# Revit family: ES – eSconce
name_source: partatom
category: Lighting Fixtures
revit_build: Autodesk Revit 2013 (Build: 20120221_2030(x64)
units: mm (PartAtom-declared; Revit-internal decimal feet)

## types (8) — shared parameters
Apparent Load = 55 VA
Default Elevation = 4' - 0"
Description = AAL's eSconce®, is has the flexibility to complement a wide range of architecture for use in both exterior/interior environments.
Glass = Hubbell - Glass
IES File Link = http://www.aal.net
Input Power = 55 W
Lamp = LED
Load Classification = Lighting
Manufacturer = Architectural Area Lighting
Model = ES-eSconce
Power Factor = 1
Product Documentation Link = http://www.aal.net
Product Page URL = http://www.aal.net
URL = http://www.aal.net
Voltage = 120 V
Wattage Comments = 37W,55W

## per-type parameters (varying)
| type | Center Panel | Panel | Photometric Web |
| Arctic White | Panel : SM4 | Hubbell - Arctic White | Web : ES3-54LED-WWX |
| Black | Panel : SM4 | Hubbell - Black | Web : ES3-54LED-WWX |
| Matte Black | Panel : SM4 | Hubbell - Matte Black | Web : ES3-54LED-WWX |
| Dark Bronze | Panel : SM4 | Hubbell - Dark Bronze | Web : ES3-54LED-WWX |
| Dark Green | Panel : SM4 | Hubbell - Dark Green | Web : ES3-54LED-WWX |
| Titanium | Panel : SM4 | Hubbell - Titanium | Web : ES3-54LED-WWX |
| Verde Blue | Panel : SMP | Hubbell - Verde Blue | Web : ES3-36LED-BW |
| Light Grey | Panel : SM4 | Hubbell - Light Grey | Web : ES3-54LED-WWX |

## geometry (parser evidence)
native form markers: Blend x17, Sweep x6
no freeform markers — native parametric forms only
